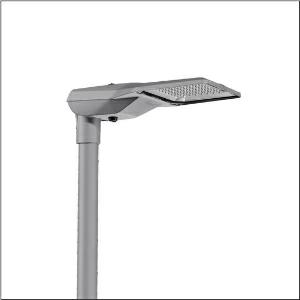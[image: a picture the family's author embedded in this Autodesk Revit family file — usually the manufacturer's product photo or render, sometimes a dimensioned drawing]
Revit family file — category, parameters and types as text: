
# Revit family: streetlight_sl_21_midi___st0_8a_5xe3c43t08lb_a4d4
name_source: partatom
category: Lighting Fixtures
units: mm (PartAtom-declared; Revit-internal decimal feet)

## family parameters
Cut with Voids When Loaded = No
Host = Face
Light Source = No
Part Type = Normal
Room Calculation Point = No
Round Connector Dimension = Use Diameter
Shared = No

## types (1)
- --- (1 x LED, 14950 lm, 98.3 W, 4000K)
    Apparent Load = 98 VA
    CIE Flux Codes = 38 75 97 100 100
    Color Rendering = 70
    Color Temperature = 4000K
    Default Elevation = 1800 mm
    Description = Streetlight SL 21 midi, mast luminaire, primary light control with lens, of PMMA, primary optical cover: cover, of toughened safety glass, transparent, light distribution: ST0.8a, light emission: direct distribution, primary light characteristic: asymmetric, installation type: side-entry, post-top, LED, High Power LED, rated luminous flux: 14.950lm, luminous efficacy: 152lm/W, light colour: 740, colour temperature: 4000K, control: overheat protection, constant luminous flux control, time-dependent luminous flux control, flexible luminous flux parameterisation, presetting dimming logarithmic, mains connection: 230..240V, AC, 50/60Hz, start of lifetime: 98W, end of service life: 101W, reduction: 45W, luminaire housing, of diecast aluminium, powder-coated, Siteco® metallic grey (DB 702S), corrosivity category C5 mid according to DIN EN ISO 12944, please order mast flange separately, inclination adjustable: 0°, 5°, 10°, 15°, sealing non-destructively replaceable, multi-level sealing system, length: 644mm, width: 335mm, height: 110mm, mast flange for spigot size: 42mm (side-entry): 5XC10008XM4, 60/48mm (side-entry/post-top): 5XC10108XM2, 76/60mm (side-entry/post-top): 5XC10108XM1, Smart Interface below and above, protection rating (complete): IP66, insulation class (complete): insulation class II (safety insulation), certification: CE, ENEC, ENEC+, VDE, impact resistance: IK09, permissible operating ambient temperature for outdoor applications: -40..+50°C, standard-compliant lighting for roads and squares, packaging unit: 1 piece

Light Distribution: ST0.8a
    Height = 111 mm
    Lamp = 1 x LED
    Lamp Light Flux = 14950 lm
    Lamp Power = 98.3 W
    Lamp count = 1
    Length = 644 mm
    Luminous efficacy = 152 lm/W
    Manufacturer = Siteco
    ModVariant = No
    Model = 5XE3C43T08LB
    Number of Poles = 1
    OnlyDefault = Yes
    Power Factor = 1
    Product Name = Streetlight SL 21 midi | ST0.8a
    Product group = mast luminaire | pylon top
    ProductGroupID = 6100
    Protection Class = Protection class II
    Protection Degree = IP 66
    RLX_Detail_Level = 1
    RLX_Emergency_Light_Flux = 0 lm
    RLX_Emergency_Type = 0
    RLX_Emergency_Type_DB = No
    RlxData = <blob elided: 92361 chars, md5=7f03850b>
    Socket = socket
    Standby Power = 0 W
    System Light Flux = 14950 lm
    System Power = 98 W
    Type Comments = factory setting: luminous flux: 100 % | dim-lin: 254 | 1020 mA
    Type Image = l_1004304.jpg
    URL = http://relux.com
    VarID = @adj_137707
    Voltage = 0 V
    Weight = 0.00 kg
    Width = 336 mm

## geometry (parser evidence)
native form markers: Blend x4, Sweep x9
no freeform markers — native parametric forms only
